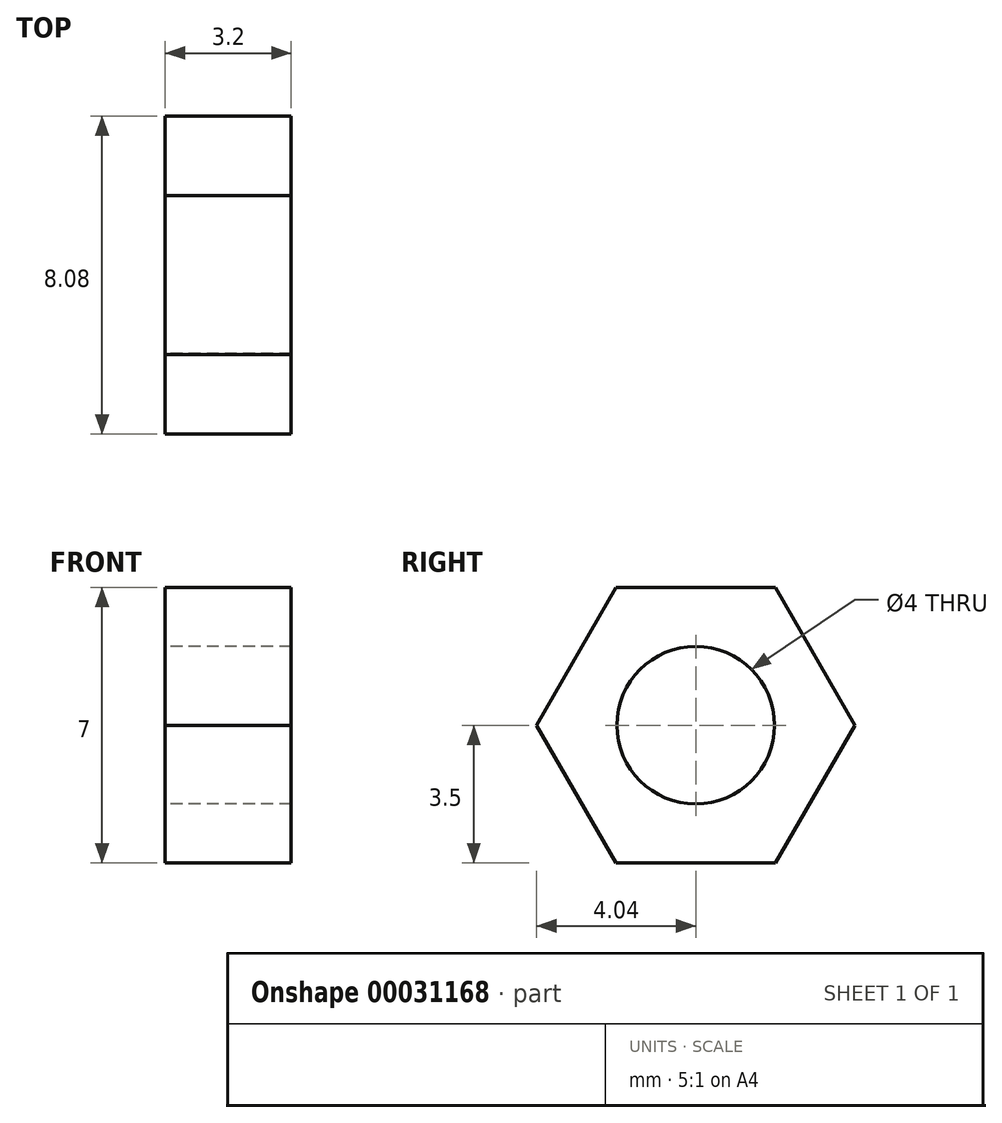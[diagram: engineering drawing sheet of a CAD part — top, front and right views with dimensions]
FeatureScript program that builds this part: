
annotation { "Feature Type Name" : "Feature", "Feature Type Description" : "" }
export const myFeature = defineFeature(function(context is Context, id is Id, definition is map)
    precondition{}
    {
        {
            var Q0;
            Q0=qCreatedBy(makeId("Right.planeOp"),FACE);
            var sketch = newSketch(context, id + "F0", { "sketchPlane" : qUnion([Q0])});
            skCircle(sketch, "E0.cCircle", {"center": v(0, 0) * mm, "radius": 3.5 * mm, "construction": true});
            skLineSegment(sketch, "E0.0", {"start": v(-2.02, 3.5) * mm, "end": v(2.02, 3.5) * mm});
            skLineSegment(sketch, "E0.1", {"start": v(2.02, 3.5) * mm, "end": v(4.04, 0) * mm});
            skLineSegment(sketch, "E0.2", {"start": v(4.04, 0) * mm, "end": v(2.02, -3.5) * mm});
            skLineSegment(sketch, "E0.3", {"start": v(2.02, -3.5) * mm, "end": v(-2.02, -3.5) * mm});
            skLineSegment(sketch, "E0.4", {"start": v(-2.02, -3.5) * mm, "end": v(-4.04, 0) * mm});
            skLineSegment(sketch, "E0.5", {"start": v(-4.04, 0) * mm, "end": v(-2.02, 3.5) * mm});
            skPoint(sketch, "E0.0.midPoint", {"position": v(0, 3.5) * mm});
            skCircle(sketch, "E1", {"center": v(0, 0) * mm, "radius": 2 * mm});
            skSolve(sketch);
        }
        {
            var Q0;
            Q0 = qSketchRegion(id + "F0", true);
            extrude(context, id + "F1", {"entities" : qUnion([Q0]), "depth" : 3.2 * mm});
        }
    });
